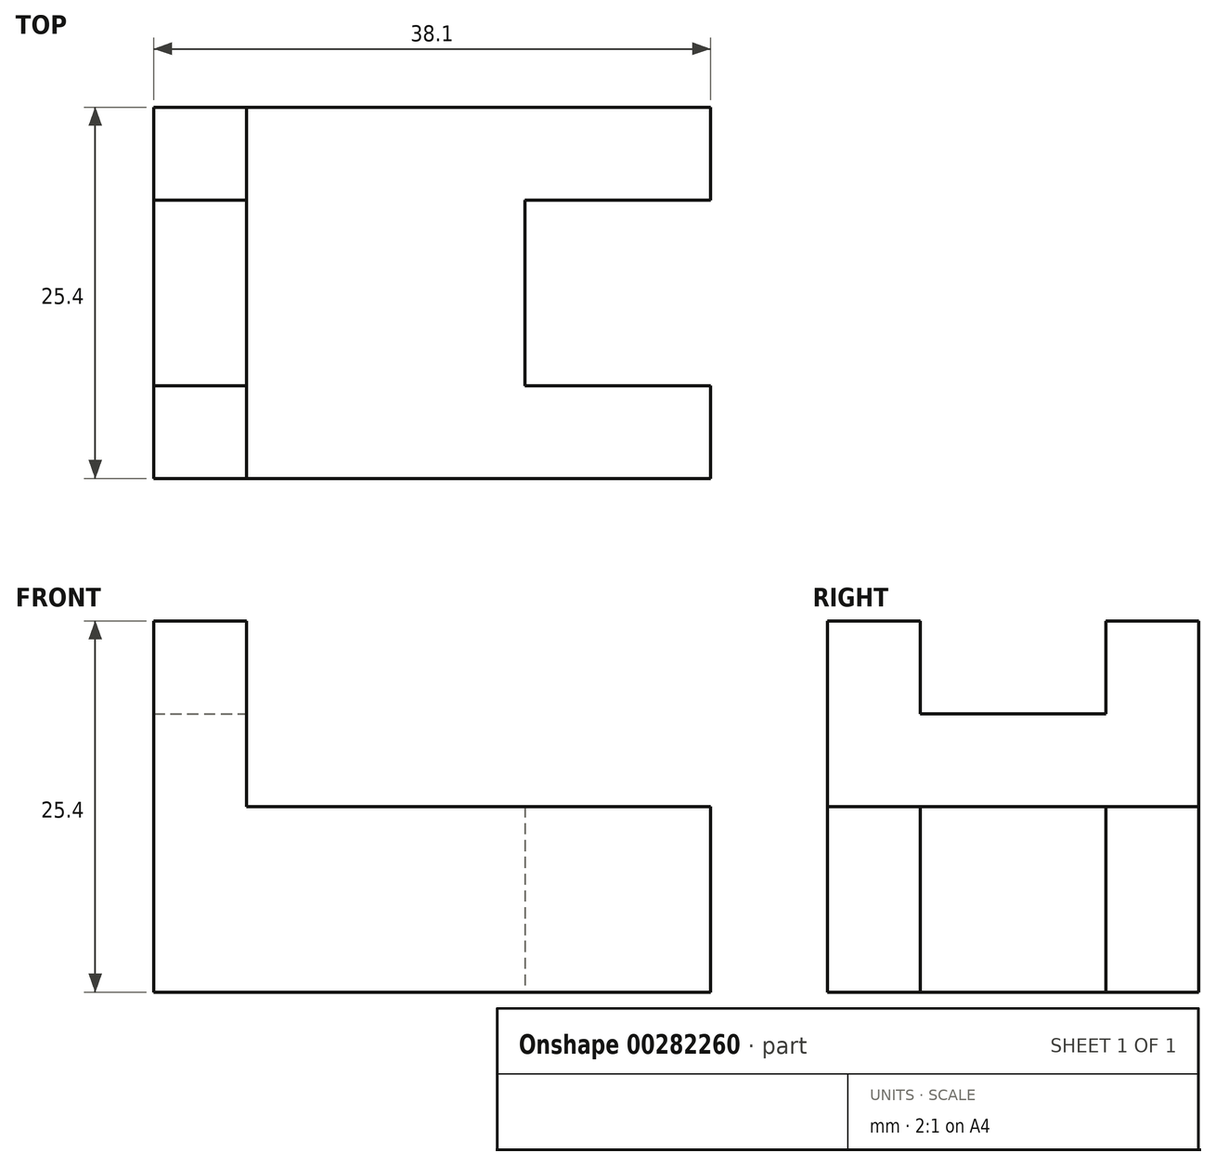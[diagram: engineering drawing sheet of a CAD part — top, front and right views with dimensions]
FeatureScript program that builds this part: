
annotation { "Feature Type Name" : "Feature", "Feature Type Description" : "" }
export const myFeature = defineFeature(function(context is Context, id is Id, definition is map)
    precondition{}
    {
        {
            var Q0;
            Q0=qCreatedBy(makeId("Front.planeOp"),FACE);
            var sketch = newSketch(context, id + "F0", { "sketchPlane" : qUnion([Q0])});
            skLineSegment(sketch, "E0.bottom", {"start": v(0, 0) * mm, "end": v(38.1, 0) * mm});
            skLineSegment(sketch, "E0.top", {"start": v(0, 12.7) * mm, "end": v(38.1, 12.7) * mm});
            skLineSegment(sketch, "E0.left", {"start": v(0, 0) * mm, "end": v(0, 12.7) * mm});
            skLineSegment(sketch, "E0.right", {"start": v(38.1, 0) * mm, "end": v(38.1, 12.7) * mm});
            skSolve(sketch);
        }
        {
            var Q0;
            Q0 = qSketchRegion(id + "F0", true);
            extrude(context, id + "F1", {"entities" : qUnion([Q0]), "endBound" : BoundingType.SYMMETRIC, "depth" : 25.4 * mm});
        }
        {
            var Q0;
            Q0=makeQuery(id+"F1.opExtrude","SWEPT_FACE",FACE,{"disambiguationData":[OSD([sQuery(id+"F0.wireOp",EDGE,"E0.top")])]});
            var sketch = newSketch(context, id + "F2", { "sketchPlane" : qUnion([Q0])});
            skLineSegment(sketch, "E1.bottom", {"start": v(0, 12.7) * mm, "end": v(6.35, 12.7) * mm});
            skLineSegment(sketch, "E1.top", {"start": v(0, -12.7) * mm, "end": v(6.35, -12.7) * mm});
            skLineSegment(sketch, "E1.left", {"start": v(0, 12.7) * mm, "end": v(0, -12.7) * mm});
            skLineSegment(sketch, "E1.right", {"start": v(6.35, 12.7) * mm, "end": v(6.35, -12.7) * mm});
            skSolve(sketch);
        }
        {
            var Q0;
            Q0 = qSketchRegion(id + "F2", true);
            extrude(context, id + "F3", {"entities" : qUnion([Q0]), "operationType" : NewBodyOperationType.ADD, "depth" : 12.7 * mm});
        }
        {
            var Q0;
            Q0=qCreatedBy(makeId("Front.planeOp"),FACE);
            var sketch = newSketch(context, id + "F4", { "sketchPlane" : qUnion([Q0])});
            skLineSegment(sketch, "E2.bottom", {"start": v(38.1, 12.7) * mm, "end": v(25.4, 12.7) * mm});
            skLineSegment(sketch, "E2.top", {"start": v(38.1, 0) * mm, "end": v(25.4, 0) * mm});
            skLineSegment(sketch, "E2.left", {"start": v(38.1, 12.7) * mm, "end": v(38.1, 0) * mm});
            skLineSegment(sketch, "E2.right", {"start": v(25.4, 12.7) * mm, "end": v(25.4, 0) * mm});
            skSolve(sketch);
        }
        {
            var Q0;
            Q0 = qSketchRegion(id + "F4", true);
            extrude(context, id + "F5", {"entities" : qUnion([Q0]), "operationType" : NewBodyOperationType.REMOVE, "endBound" : BoundingType.SYMMETRIC, "depth" : 12.7 * mm});
        }
        {
            var Q0;
            Q0=qCreatedBy(makeId("Front.planeOp"),FACE);
            var sketch = newSketch(context, id + "F6", { "sketchPlane" : qUnion([Q0])});
            skLineSegment(sketch, "E3.bottom", {"start": v(0, 25.4) * mm, "end": v(6.35, 25.4) * mm});
            skLineSegment(sketch, "E3.top", {"start": v(0, 19.05) * mm, "end": v(6.35, 19.05) * mm});
            skLineSegment(sketch, "E3.left", {"start": v(0, 25.4) * mm, "end": v(0, 19.05) * mm});
            skLineSegment(sketch, "E3.right", {"start": v(6.35, 25.4) * mm, "end": v(6.35, 19.05) * mm});
            skSolve(sketch);
        }
        {
            var Q0;
            Q0 = qSketchRegion(id + "F6", true);
            extrude(context, id + "F7", {"entities" : qUnion([Q0]), "operationType" : NewBodyOperationType.REMOVE, "endBound" : BoundingType.SYMMETRIC, "depth" : 12.7 * mm});
        }
    });
